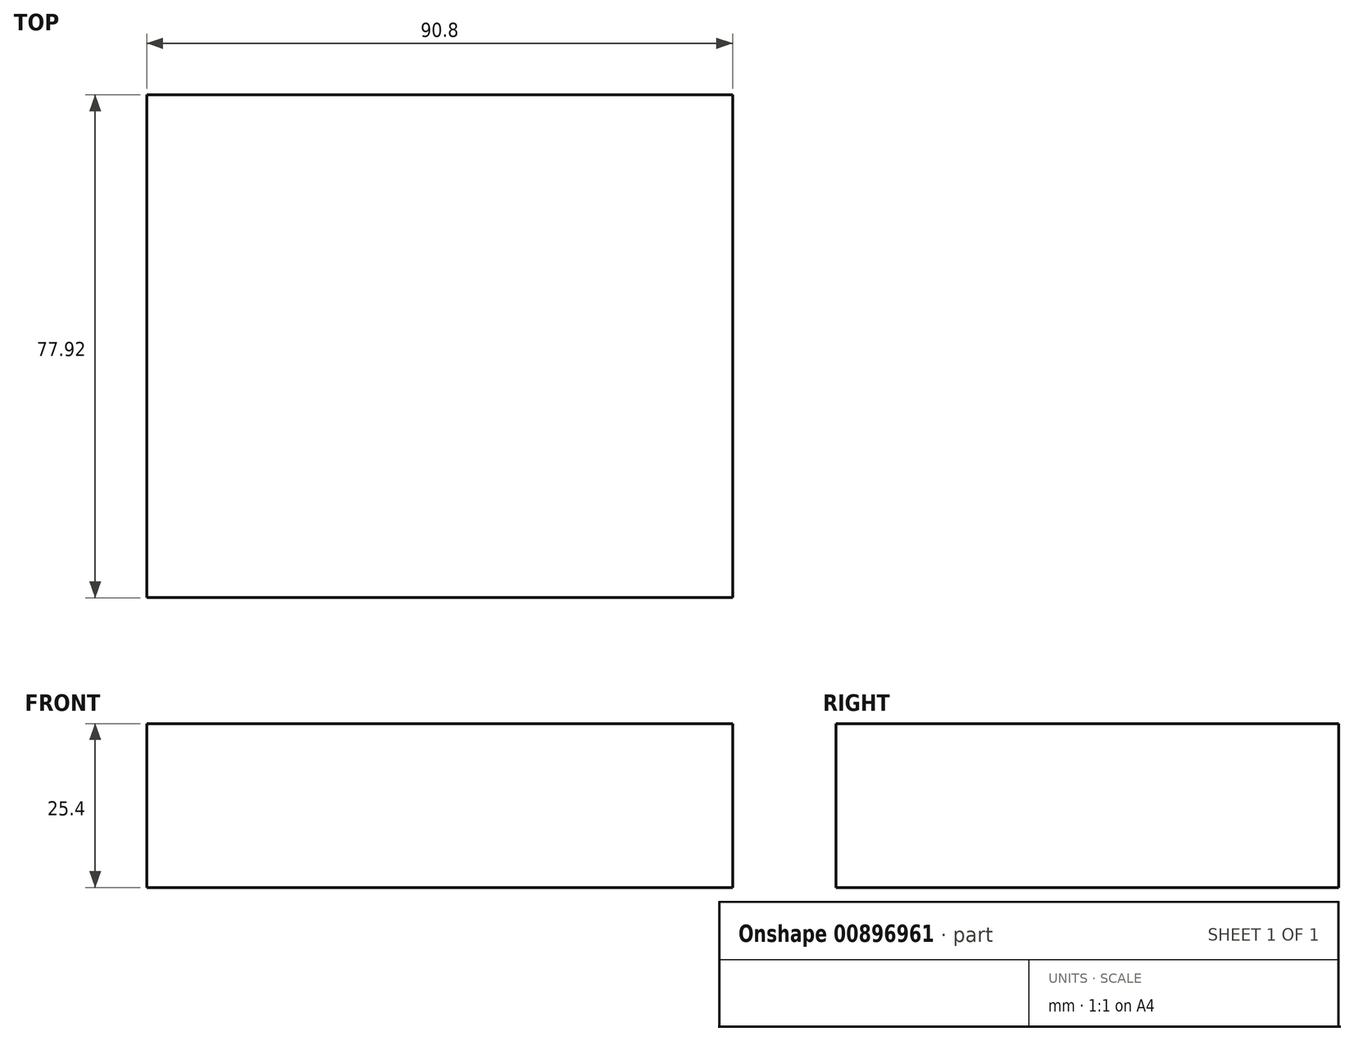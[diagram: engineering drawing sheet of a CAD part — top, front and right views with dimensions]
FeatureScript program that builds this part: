
annotation { "Feature Type Name" : "Feature", "Feature Type Description" : "" }
export const myFeature = defineFeature(function(context is Context, id is Id, definition is map)
    precondition{}
    {
        {
            var Q0;
            Q0=qCreatedBy(makeId("Top.planeOp"),FACE);
            var sketch = newSketch(context, id + "F0", { "sketchPlane" : qUnion([Q0])});
            skLineSegment(sketch, "E0.bottom", {"start": v(30.76, -16.9) * mm, "end": v(-60.04, -16.9) * mm});
            skLineSegment(sketch, "E0.top", {"start": v(30.76, 61.01) * mm, "end": v(-60.04, 61.01) * mm});
            skLineSegment(sketch, "E0.left", {"start": v(30.76, -16.9) * mm, "end": v(30.76, 61.01) * mm});
            skLineSegment(sketch, "E0.right", {"start": v(-60.04, -16.9) * mm, "end": v(-60.04, 61.01) * mm});
            skSolve(sketch);
        }
        {
            var Q0;
            Q0=makeQuery(id+"F0.imprint","IMPRINT",FACE,{"disambiguationData":[TD([[makeQuery(id+"F0.imprint","IMPRINT",EDGE,{"derivedFrom":sQuery(id+"F0.wireOp",EDGE,"E0.bottom")}),-1.0]])]});
            extrude(context, id + "F1", {"entities" : qUnion([Q0]), "depth" : 25.4 * mm, "offsetDistance" : 25.4 * mm});
        }
    });
